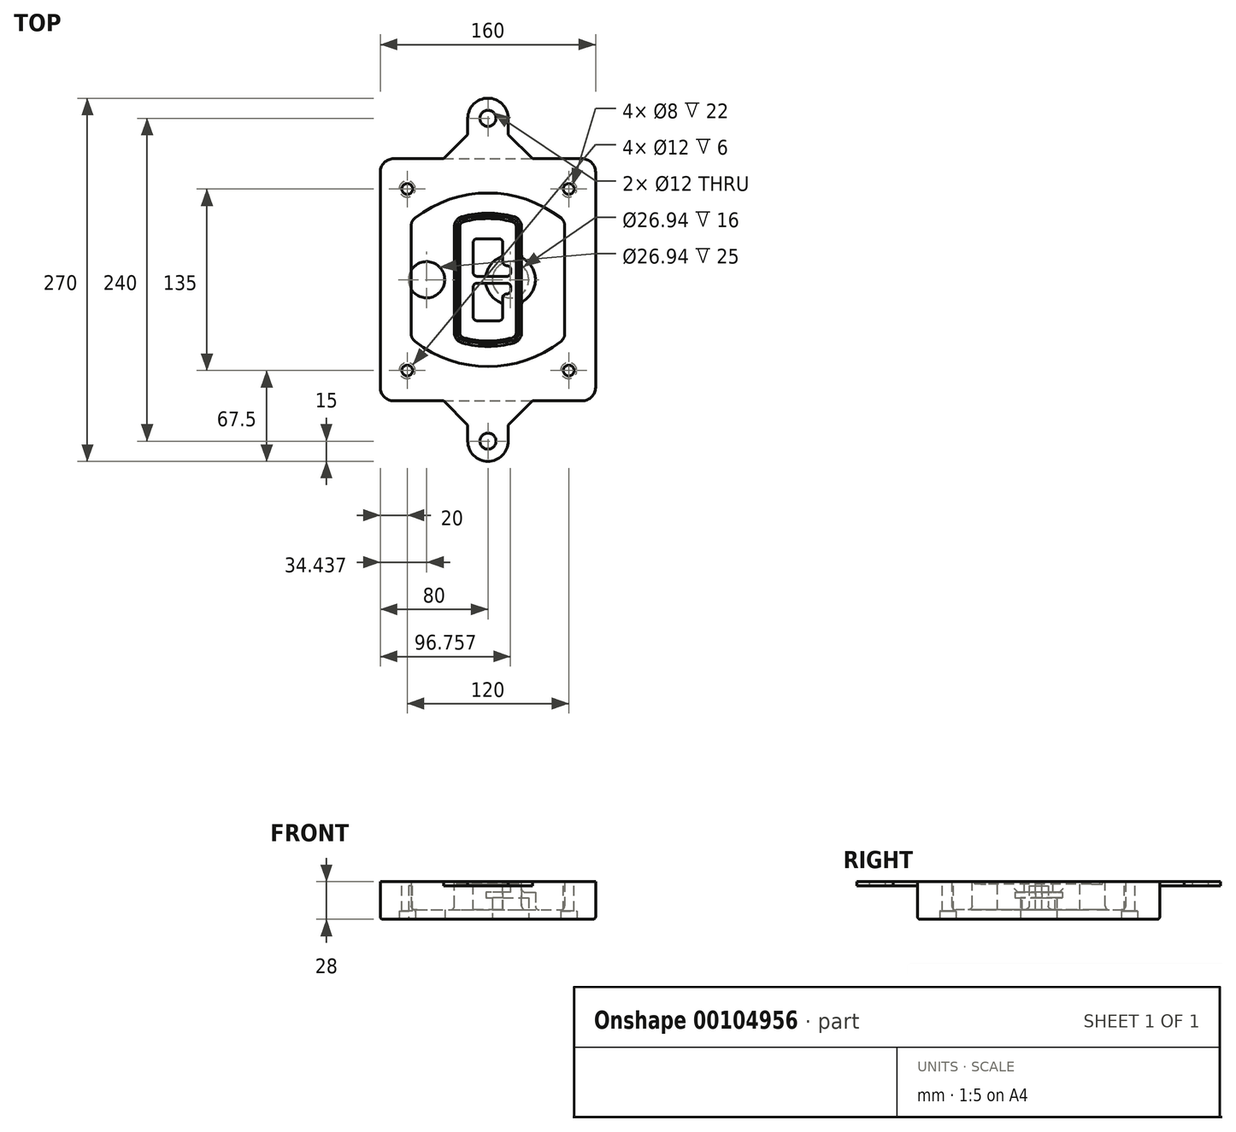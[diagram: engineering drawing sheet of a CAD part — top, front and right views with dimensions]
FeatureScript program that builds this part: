
annotation { "Feature Type Name" : "Feature", "Feature Type Description" : "" }
export const myFeature = defineFeature(function(context is Context, id is Id, definition is map)
    precondition{}
    {
        {
            var Q0;
            Q0=qCreatedBy(makeId("Top.planeOp"),FACE);
            var sketch = newSketch(context, id + "F0", { "sketchPlane" : qUnion([Q0])});
            skPoint(sketch, "E0.rect.middle", {"position": v(0, 0) * mm});
            skLineSegment(sketch, "E1.bottom", {"start": v(-70, -90) * mm, "end": v(70, -90) * mm});
            skLineSegment(sketch, "E1.top", {"start": v(-70, 90) * mm, "end": v(70, 90) * mm});
            skLineSegment(sketch, "E1.left", {"start": v(-80, -80) * mm, "end": v(-80, 80) * mm});
            skLineSegment(sketch, "E1.right", {"start": v(80, -80) * mm, "end": v(80, 80) * mm});
            skLineSegment(sketch, "E2", {"start": v(-80, 90) * mm, "end": v(80, -90) * mm, "construction": true});
            skLineSegment(sketch, "E3", {"start": v(80, 90) * mm, "end": v(-80, -90) * mm, "construction": true});
            skCircle(sketch, "E4", {"center": v(-60, 67.5) * mm, "radius": 4 * mm});
            skCircle(sketch, "E5", {"center": v(60, 67.5) * mm, "radius": 4 * mm});
            skCircle(sketch, "E6", {"center": v(60, -67.5) * mm, "radius": 4 * mm});
            skCircle(sketch, "E7", {"center": v(-60, -67.5) * mm, "radius": 4 * mm});
            skLineSegment(sketch, "E8", {"start": v(-60, 67.5) * mm, "end": v(60, 67.5) * mm, "construction": true});
            skLineSegment(sketch, "E9", {"start": v(60, 67.5) * mm, "end": v(60, -67.5) * mm, "construction": true});
            skLineSegment(sketch, "E10", {"start": v(60, -67.5) * mm, "end": v(-60, -67.5) * mm, "construction": true});
            skLineSegment(sketch, "E11", {"start": v(-60, -67.5) * mm, "end": v(-60, 67.5) * mm, "construction": true});
            skLineSegment(sketch, "E12", {"start": v(-60, 40.3) * mm, "end": v(-60, -40.3) * mm});
            skLineSegment(sketch, "E13", {"start": v(60, 40.3) * mm, "end": v(60, -40.3) * mm});
            skArc(sketch, "E14", {"start": v(56.15, 48.18) * mm, "mid": v(0, 67.5) * mm, "end": v(-56.15, 48.18) * mm});
            skArc(sketch, "E15", {"start": v(-56.15, -48.18) * mm, "mid": v(0, -67.5) * mm, "end": v(56.15, -48.18) * mm});
            skLineSegment(sketch, "E16", {"start": v(-60, 0) * mm, "end": v(60, 0) * mm, "construction": true});
            skPoint(sketch, "E17.visualSharp", {"position": v(-60, -45) * mm});
            skArc(sketch, "E17.filletArc", {"start": v(-60, -40.3) * mm, "mid": v(-58.99, -44.68) * mm, "end": v(-56.15, -48.18) * mm});
            skPoint(sketch, "E18.visualSharp", {"position": v(-60, 45) * mm});
            skArc(sketch, "E18.filletArc", {"start": v(-56.15, 48.18) * mm, "mid": v(-58.99, 44.68) * mm, "end": v(-60, 40.3) * mm});
            skPoint(sketch, "E19.visualSharp", {"position": v(60, 45) * mm});
            skArc(sketch, "E19.filletArc", {"start": v(60, 40.3) * mm, "mid": v(58.99, 44.68) * mm, "end": v(56.15, 48.18) * mm});
            skPoint(sketch, "E20.visualSharp", {"position": v(60, -45) * mm});
            skArc(sketch, "E20.filletArc", {"start": v(56.15, -48.18) * mm, "mid": v(58.99, -44.68) * mm, "end": v(60, -40.3) * mm});
            skPoint(sketch, "E21.visualSharp", {"position": v(-80, 90) * mm});
            skArc(sketch, "E21.filletArc", {"start": v(-70, 90) * mm, "mid": v(-77.07, 87.07) * mm, "end": v(-80, 80) * mm});
            skPoint(sketch, "E22.visualSharp", {"position": v(80, 90) * mm});
            skArc(sketch, "E22.filletArc", {"start": v(80, 80) * mm, "mid": v(77.07, 87.07) * mm, "end": v(70, 90) * mm});
            skPoint(sketch, "E23.visualSharp", {"position": v(80, -90) * mm});
            skArc(sketch, "E23.filletArc", {"start": v(70, -90) * mm, "mid": v(77.07, -87.07) * mm, "end": v(80, -80) * mm});
            skPoint(sketch, "E24.visualSharp", {"position": v(-80, -90) * mm});
            skArc(sketch, "E24.filletArc", {"start": v(-80, -80) * mm, "mid": v(-77.07, -87.07) * mm, "end": v(-70, -90) * mm});
            skArc(sketch, "E25.0", {"start": v(57, 40.3) * mm, "mid": v(56.3, 43.36) * mm, "end": v(54.3, 45.81) * mm});
            skLineSegment(sketch, "E25.1", {"start": v(57, 40.3) * mm, "end": v(57, -40.3) * mm});
            skArc(sketch, "E25.2", {"start": v(54.3, -45.81) * mm, "mid": v(56.3, -43.36) * mm, "end": v(57, -40.3) * mm});
            skArc(sketch, "E25.3", {"start": v(-54.3, -45.81) * mm, "mid": v(0, -64.5) * mm, "end": v(54.3, -45.81) * mm});
            skArc(sketch, "E25.4", {"start": v(-57, -40.3) * mm, "mid": v(-56.3, -43.36) * mm, "end": v(-54.3, -45.81) * mm});
            skArc(sketch, "E25.5", {"start": v(54.3, 45.81) * mm, "mid": v(0, 64.5) * mm, "end": v(-54.3, 45.81) * mm});
            skLineSegment(sketch, "E25.6", {"start": v(-57, 40.3) * mm, "end": v(-57, -40.3) * mm});
            skArc(sketch, "E25.7", {"start": v(-54.3, 45.81) * mm, "mid": v(-56.3, 43.36) * mm, "end": v(-57, 40.3) * mm});
            skArc(sketch, "E26.0", {"start": v(-58.62, 51.33) * mm, "mid": v(-62.58, 46.43) * mm, "end": v(-64, 40.3) * mm});
            skArc(sketch, "E26.1", {"start": v(58.62, 51.33) * mm, "mid": v(0, 71.5) * mm, "end": v(-58.62, 51.33) * mm});
            skArc(sketch, "E26.2", {"start": v(64, 40.3) * mm, "mid": v(62.58, 46.43) * mm, "end": v(58.62, 51.33) * mm});
            skLineSegment(sketch, "E26.3", {"start": v(64, 40.3) * mm, "end": v(64, -40.3) * mm});
            skArc(sketch, "E26.4", {"start": v(58.62, -51.33) * mm, "mid": v(62.58, -46.43) * mm, "end": v(64, -40.3) * mm});
            skLineSegment(sketch, "E26.5", {"start": v(-64, 40.3) * mm, "end": v(-64, -40.3) * mm});
            skArc(sketch, "E26.6", {"start": v(-58.62, -51.33) * mm, "mid": v(0, -71.5) * mm, "end": v(58.62, -51.33) * mm});
            skArc(sketch, "E26.7", {"start": v(-64, -40.3) * mm, "mid": v(-62.58, -46.43) * mm, "end": v(-58.62, -51.33) * mm});
            skSolve(sketch);
        }
        {
            var Q0;
            Q0=makeQuery(id+"F0.imprint","IMPRINT",FACE,{"disambiguationData":[TD([[makeQuery(id+"F0.imprint","IMPRINT",EDGE,{"derivedFrom":sQuery(id+"F0.wireOp",EDGE,"E1.bottom")}),1.0]])]});
            var Q1;
            Q1=makeQuery(id+"F0.imprint","IMPRINT",FACE,{"disambiguationData":[TD([[makeQuery(id+"F0.imprint","IMPRINT",EDGE,{"derivedFrom":sQuery(id+"F0.wireOp",EDGE,"E12")}),1.0]])]});
            var Q2;
            Q2=makeQuery(id+"F0.imprint","IMPRINT",FACE,{"disambiguationData":[TD([[makeQuery(id+"F0.imprint","IMPRINT",EDGE,{"derivedFrom":sQuery(id+"F0.wireOp",EDGE,"E25.0")}),1.0]])]});
            var Q3;
            Q3=makeQuery(id+"F0.imprint","IMPRINT",FACE,{"disambiguationData":[TD([[makeQuery(id+"F0.imprint","IMPRINT",EDGE,{"derivedFrom":sQuery(id+"F0.wireOp",EDGE,"E12")}),-1.0]])]});
            extrude(context, id + "F1", {"entities" : qUnion([Q0, Q1, Q2, Q3]), "oppositeDirection" : true, "depth" : 25 * mm});
        }
        {
            var Q0;
            Q0=makeQuery(id+"F0.imprint","IMPRINT",FACE,{"disambiguationData":[TD([[makeQuery(id+"F0.imprint","IMPRINT",EDGE,{"derivedFrom":sQuery(id+"F0.wireOp",EDGE,"E12")}),1.0]])]});
            extrude(context, id + "F2", {"entities" : qUnion([Q0]), "operationType" : NewBodyOperationType.ADD, "depth" : 3 * mm});
        }
        {
            var Q0;
            Q0=makeQuery(id+"F0.imprint","IMPRINT",FACE,{"disambiguationData":[TD([[makeQuery(id+"F0.imprint","IMPRINT",EDGE,{"derivedFrom":sQuery(id+"F0.wireOp",EDGE,"E25.0")}),1.0]])]});
            extrude(context, id + "F3", {"entities" : qUnion([Q0]), "operationType" : NewBodyOperationType.REMOVE, "oppositeDirection" : true, "depth" : 18 * mm});
        }
        {
            var Q0;
            Q0=makeQuery(id+"F2.opExtrude","CAP_FACE",FACE,{"disambiguationData":[OSD([sQuery(id+"F0.wireOp",EDGE,"E12"),sQuery(id+"F0.wireOp",EDGE,"E13"),sQuery(id+"F0.wireOp",EDGE,"E14"),sQuery(id+"F0.wireOp",EDGE,"E15"),sQuery(id+"F0.wireOp",EDGE,"E17.filletArc"),sQuery(id+"F0.wireOp",EDGE,"E18.filletArc"),sQuery(id+"F0.wireOp",EDGE,"E19.filletArc"),sQuery(id+"F0.wireOp",EDGE,"E20.filletArc"),sQuery(id+"F0.wireOp",EDGE,"E25.0"),sQuery(id+"F0.wireOp",EDGE,"E25.1"),sQuery(id+"F0.wireOp",EDGE,"E25.2"),sQuery(id+"F0.wireOp",EDGE,"E25.3"),sQuery(id+"F0.wireOp",EDGE,"E25.4"),sQuery(id+"F0.wireOp",EDGE,"E25.5"),sQuery(id+"F0.wireOp",EDGE,"E25.6"),sQuery(id+"F0.wireOp",EDGE,"E25.7")])],"isStart":false});
            var sketch = newSketch(context, id + "F4", { "sketchPlane" : qUnion([Q0])});
            skArc(sketch, "E27.0", {"start": v(-19.08, -46.97) * mm, "mid": v(0, -49.5) * mm, "end": v(19.08, -46.97) * mm});
            skArc(sketch, "E28.0", {"start": v(19.08, 46.97) * mm, "mid": v(0, 49.5) * mm, "end": v(-19.08, 46.97) * mm});
            skLineSegment(sketch, "E29", {"start": v(-25, 39.25) * mm, "end": v(-25, -39.25) * mm});
            skLineSegment(sketch, "E30", {"start": v(25, 39.25) * mm, "end": v(25, -39.25) * mm});
            skLineSegment(sketch, "E31", {"start": v(-25, 45.1) * mm, "end": v(25, 45.1) * mm, "construction": true});
            skLineSegment(sketch, "E32", {"start": v(-25, -45.1) * mm, "end": v(25, -45.1) * mm, "construction": true});
            skPoint(sketch, "E33.visualSharp", {"position": v(-25, 45.1) * mm});
            skArc(sketch, "E33.filletArc", {"start": v(-19.08, 46.97) * mm, "mid": v(-23.35, 44.11) * mm, "end": v(-25, 39.25) * mm});
            skPoint(sketch, "E34.visualSharp", {"position": v(25, 45.1) * mm});
            skArc(sketch, "E34.filletArc", {"start": v(25, 39.25) * mm, "mid": v(23.35, 44.11) * mm, "end": v(19.08, 46.97) * mm});
            skPoint(sketch, "E35.visualSharp", {"position": v(25, -45.1) * mm});
            skArc(sketch, "E35.filletArc", {"start": v(19.08, -46.97) * mm, "mid": v(23.35, -44.11) * mm, "end": v(25, -39.25) * mm});
            skPoint(sketch, "E36.visualSharp", {"position": v(-25, -45.1) * mm});
            skArc(sketch, "E36.filletArc", {"start": v(-25, -39.25) * mm, "mid": v(-23.35, -44.11) * mm, "end": v(-19.08, -46.97) * mm});
            skArc(sketch, "E37.0", {"start": v(54.3, 45.81) * mm, "mid": v(0, 64.5) * mm, "end": v(-54.3, 45.81) * mm});
            skArc(sketch, "E37.1", {"start": v(-54.3, 45.81) * mm, "mid": v(-56.3, 43.36) * mm, "end": v(-57, 40.3) * mm});
            skLineSegment(sketch, "E37.2", {"start": v(-57, 40.3) * mm, "end": v(-57, -40.3) * mm});
            skArc(sketch, "E37.3", {"start": v(-57, -40.3) * mm, "mid": v(-56.3, -43.36) * mm, "end": v(-54.3, -45.81) * mm});
            skArc(sketch, "E37.4", {"start": v(-54.3, -45.81) * mm, "mid": v(0, -64.5) * mm, "end": v(54.3, -45.81) * mm});
            skArc(sketch, "E37.5", {"start": v(54.3, -45.81) * mm, "mid": v(56.3, -43.36) * mm, "end": v(57, -40.3) * mm});
            skLineSegment(sketch, "E37.6", {"start": v(57, 40.3) * mm, "end": v(57, -40.3) * mm});
            skArc(sketch, "E37.7", {"start": v(57, 40.3) * mm, "mid": v(56.3, 43.36) * mm, "end": v(54.3, 45.81) * mm});
            skLineSegment(sketch, "E38.0", {"start": v(23, 39.25) * mm, "end": v(23, -39.25) * mm});
            skArc(sketch, "E38.1", {"start": v(18.56, -45.04) * mm, "mid": v(21.76, -42.9) * mm, "end": v(23, -39.25) * mm});
            skArc(sketch, "E38.2", {"start": v(-18.56, -45.04) * mm, "mid": v(0, -47.5) * mm, "end": v(18.56, -45.04) * mm});
            skArc(sketch, "E38.3", {"start": v(-23, -39.25) * mm, "mid": v(-21.76, -42.9) * mm, "end": v(-18.56, -45.04) * mm});
            skLineSegment(sketch, "E38.4", {"start": v(-23, 39.25) * mm, "end": v(-23, -39.25) * mm});
            skArc(sketch, "E38.5", {"start": v(23, 39.25) * mm, "mid": v(21.76, 42.9) * mm, "end": v(18.56, 45.04) * mm});
            skArc(sketch, "E38.6", {"start": v(-18.56, 45.04) * mm, "mid": v(-21.76, 42.9) * mm, "end": v(-23, 39.25) * mm});
            skArc(sketch, "E38.7", {"start": v(18.56, 45.04) * mm, "mid": v(0, 47.5) * mm, "end": v(-18.56, 45.04) * mm});
            skArc(sketch, "E39.0", {"start": v(21, 39.25) * mm, "mid": v(20.18, 41.68) * mm, "end": v(18.04, 43.1) * mm});
            skLineSegment(sketch, "E39.1", {"start": v(21, 39.25) * mm, "end": v(21, -39.25) * mm});
            skArc(sketch, "E39.2", {"start": v(18.04, -43.1) * mm, "mid": v(20.18, -41.68) * mm, "end": v(21, -39.25) * mm});
            skArc(sketch, "E39.3", {"start": v(-18.04, -43.1) * mm, "mid": v(0, -45.5) * mm, "end": v(18.04, -43.1) * mm});
            skArc(sketch, "E39.4", {"start": v(-21, -39.25) * mm, "mid": v(-20.18, -41.68) * mm, "end": v(-18.04, -43.1) * mm});
            skArc(sketch, "E39.5", {"start": v(18.04, 43.1) * mm, "mid": v(0, 45.5) * mm, "end": v(-18.04, 43.1) * mm});
            skLineSegment(sketch, "E39.6", {"start": v(-21, 39.25) * mm, "end": v(-21, -39.25) * mm});
            skArc(sketch, "E39.7", {"start": v(-18.04, 43.1) * mm, "mid": v(-20.18, 41.68) * mm, "end": v(-21, 39.25) * mm});
            skLineSegment(sketch, "E40", {"start": v(-25, 0) * mm, "end": v(25, 0) * mm, "construction": true});
            skLineSegment(sketch, "E41", {"start": v(-11, 5.5) * mm, "end": v(-11, 27.5) * mm});
            skLineSegment(sketch, "E42", {"start": v(-8, 30.5) * mm, "end": v(8, 30.5) * mm});
            skLineSegment(sketch, "E43", {"start": v(11, 27.5) * mm, "end": v(11, 13.5) * mm});
            skLineSegment(sketch, "E44", {"start": v(14, 10.5) * mm, "end": v(14, 10.5) * mm});
            skLineSegment(sketch, "E45", {"start": v(17, 7.5) * mm, "end": v(17, 5.5) * mm});
            skLineSegment(sketch, "E46", {"start": v(14, 2.5) * mm, "end": v(-8, 2.5) * mm});
            skPoint(sketch, "E47.visualSharp", {"position": v(-11, 30.5) * mm});
            skArc(sketch, "E47.filletArc", {"start": v(-8, 30.5) * mm, "mid": v(-10.12, 29.62) * mm, "end": v(-11, 27.5) * mm});
            skPoint(sketch, "E48.visualSharp", {"position": v(11, 30.5) * mm});
            skArc(sketch, "E48.filletArc", {"start": v(11, 27.5) * mm, "mid": v(10.12, 29.62) * mm, "end": v(8, 30.5) * mm});
            skPoint(sketch, "E49.visualSharp", {"position": v(11, 10.5) * mm});
            skArc(sketch, "E49.filletArc", {"start": v(11, 13.5) * mm, "mid": v(11.88, 11.38) * mm, "end": v(14, 10.5) * mm});
            skPoint(sketch, "E50.visualSharp", {"position": v(17, 10.5) * mm});
            skArc(sketch, "E50.filletArc", {"start": v(17, 7.5) * mm, "mid": v(16.12, 9.62) * mm, "end": v(14, 10.5) * mm});
            skPoint(sketch, "E51.visualSharp", {"position": v(17, 2.5) * mm});
            skArc(sketch, "E51.filletArc", {"start": v(14, 2.5) * mm, "mid": v(16.12, 3.38) * mm, "end": v(17, 5.5) * mm});
            skPoint(sketch, "E52.visualSharp", {"position": v(-11, 2.5) * mm});
            skArc(sketch, "E52.filletArc", {"start": v(-11, 5.5) * mm, "mid": v(-10.12, 3.38) * mm, "end": v(-8, 2.5) * mm});
            skLineSegment(sketch, "E53.0.MirrorCS", {"start": v(14, -2.5) * mm, "end": v(-8, -2.5) * mm});
            skArc(sketch, "E54.0.MirrorCS", {"start": v(-11, -5.5) * mm, "mid": v(-10.12, -3.38) * mm, "end": v(-8, -2.5) * mm});
            skLineSegment(sketch, "E55.0.MirrorCS", {"start": v(-11, -5.5) * mm, "end": v(-11, -27.5) * mm});
            skArc(sketch, "E56.0.MirrorCS", {"start": v(-8, -30.5) * mm, "mid": v(-10.12, -29.62) * mm, "end": v(-11, -27.5) * mm});
            skLineSegment(sketch, "E57.0.MirrorCS", {"start": v(-8, -30.5) * mm, "end": v(8, -30.5) * mm});
            skArc(sketch, "E58.0.MirrorCS", {"start": v(11, -27.5) * mm, "mid": v(10.12, -29.62) * mm, "end": v(8, -30.5) * mm});
            skLineSegment(sketch, "E59.0.MirrorCS", {"start": v(11, -27.5) * mm, "end": v(11, -13.5) * mm});
            skArc(sketch, "E60.0.MirrorCS", {"start": v(11, -13.5) * mm, "mid": v(11.88, -11.38) * mm, "end": v(14, -10.5) * mm});
            skArc(sketch, "E61.0.MirrorCS", {"start": v(17, -7.5) * mm, "mid": v(16.12, -9.62) * mm, "end": v(14, -10.5) * mm});
            skLineSegment(sketch, "E62.0.MirrorCS", {"start": v(17, -7.5) * mm, "end": v(17, -5.5) * mm});
            skArc(sketch, "E63.0.MirrorCS", {"start": v(14, -2.5) * mm, "mid": v(16.12, -3.38) * mm, "end": v(17, -5.5) * mm});
            skSolve(sketch);
        }
        {
            var Q0;
            Q0=makeQuery(id+"F4.imprint","IMPRINT",FACE,{"disambiguationData":[TD([[makeQuery(id+"F4.imprint","IMPRINT",EDGE,{"derivedFrom":sQuery(id+"F4.wireOp",EDGE,"E27.0")}),1.0]])]});
            var Q1;
            Q1=makeQuery(id+"F4.imprint","IMPRINT",FACE,{"disambiguationData":[TD([[makeQuery(id+"F4.imprint","IMPRINT",EDGE,{"derivedFrom":sQuery(id+"F4.wireOp",EDGE,"E38.0")}),-1.0]])]});
            var Q2;
            Q2=makeQuery(id+"F4.imprint","IMPRINT",FACE,{"disambiguationData":[TD([[makeQuery(id+"F4.imprint","IMPRINT",EDGE,{"derivedFrom":sQuery(id+"F4.wireOp",EDGE,"E39.0")}),1.0]])]});
            extrude(context, id + "F5", {"entities" : qUnion([Q0, Q1, Q2]), "operationType" : NewBodyOperationType.ADD, "endBound" : BoundingType.UP_TO_NEXT, "oppositeDirection" : true, "depth" : 25 * mm});
        }
        {
            var Q0;
            Q0=makeQuery(id+"F4.imprint","IMPRINT",FACE,{"disambiguationData":[TD([[makeQuery(id+"F4.imprint","IMPRINT",EDGE,{"derivedFrom":sQuery(id+"F4.wireOp",EDGE,"E38.0")}),-1.0]])]});
            extrude(context, id + "F6", {"entities" : qUnion([Q0]), "operationType" : NewBodyOperationType.REMOVE, "oppositeDirection" : true, "depth" : 2 * mm});
        }
        {
            var Q0;
            Q0=makeQuery(id+"F1.opExtrude","CAP_FACE",FACE,{"disambiguationData":[OSD([sQuery(id+"F0.wireOp",EDGE,"E1.bottom"),sQuery(id+"F0.wireOp",EDGE,"E1.top"),sQuery(id+"F0.wireOp",EDGE,"E1.left"),sQuery(id+"F0.wireOp",EDGE,"E1.right"),sQuery(id+"F0.wireOp",EDGE,"E4"),sQuery(id+"F0.wireOp",EDGE,"E5"),sQuery(id+"F0.wireOp",EDGE,"E6"),sQuery(id+"F0.wireOp",EDGE,"E7"),sQuery(id+"F0.wireOp",EDGE,"E21.filletArc"),sQuery(id+"F0.wireOp",EDGE,"E22.filletArc"),sQuery(id+"F0.wireOp",EDGE,"E23.filletArc"),sQuery(id+"F0.wireOp",EDGE,"E24.filletArc")])],"isStart":false});
            var sketch = newSketch(context, id + "F7", { "sketchPlane" : qUnion([Q0])});
            skCircle(sketch, "E64", {"center": v(16.76, 0) * mm, "radius": 13.47 * mm});
            skCircle(sketch, "E65", {"center": v(-45.56, 0) * mm, "radius": 13.47 * mm});
            skLineSegment(sketch, "E66", {"start": v(80, 0) * mm, "end": v(-80, 0) * mm});
            skCircle(sketch, "E67", {"center": v(16.76, 0) * mm, "radius": 18.47 * mm});
            skCircle(sketch, "E68", {"center": v(60, -67.5) * mm, "radius": 6 * mm});
            skCircle(sketch, "E69", {"center": v(-60, -67.5) * mm, "radius": 6 * mm});
            skCircle(sketch, "E70", {"center": v(-60, 67.5) * mm, "radius": 6 * mm});
            skCircle(sketch, "E71", {"center": v(60, 67.5) * mm, "radius": 6 * mm});
            skSolve(sketch);
        }
        {
            var Q0;
            {var subQ1=sQuery(id+"F7.wireOp",EDGE,"E66");var subQ4=sQuery(id+"F7.wireOp",EDGE,"E64");var subQ6=makeQuery(id+"F7.imprint","INTERSECT",VERTEX,{"disambiguationData":[OD(0.0)],"derivedFrom":[subQ4,subQ1]});Q0=makeQuery(id+"F7.imprint","IMPRINT",FACE,{"disambiguationData":[TD([[makeQuery(id+"F7.imprint","IMPRINT",EDGE,{"disambiguationData":[TD([[subQ6,-1.0]])],"derivedFrom":subQ4}),-1.0]])]});}
            var Q1;
            {var subQ0=sQuery(id+"F7.wireOp",EDGE,"E66");var subQ1=sQuery(id+"F7.wireOp",EDGE,"E64");var subQ3=makeQuery(id+"F7.imprint","INTERSECT",VERTEX,{"disambiguationData":[OD(0.0)],"derivedFrom":[subQ1,subQ0]});Q1=makeQuery(id+"F7.imprint","IMPRINT",FACE,{"disambiguationData":[TD([[makeQuery(id+"F7.imprint","IMPRINT",EDGE,{"disambiguationData":[TD([[subQ3,-1.0]])],"derivedFrom":subQ1}),1.0]])]});}
            var Q2;
            {var subQ0=sQuery(id+"F7.wireOp",EDGE,"E66");var subQ1=sQuery(id+"F7.wireOp",EDGE,"E64");var subQ3=makeQuery(id+"F7.imprint","INTERSECT",VERTEX,{"disambiguationData":[OD(0.0)],"derivedFrom":[subQ1,subQ0]});Q2=makeQuery(id+"F7.imprint","IMPRINT",FACE,{"disambiguationData":[TD([[makeQuery(id+"F7.imprint","IMPRINT",EDGE,{"disambiguationData":[TD([[subQ3,1.0]])],"derivedFrom":subQ1}),1.0]])]});}
            var Q3;
            {var subQ1=sQuery(id+"F7.wireOp",EDGE,"E66");var subQ4=sQuery(id+"F7.wireOp",EDGE,"E64");var subQ6=makeQuery(id+"F7.imprint","INTERSECT",VERTEX,{"disambiguationData":[OD(0.0)],"derivedFrom":[subQ4,subQ1]});Q3=makeQuery(id+"F7.imprint","IMPRINT",FACE,{"disambiguationData":[TD([[makeQuery(id+"F7.imprint","IMPRINT",EDGE,{"disambiguationData":[TD([[subQ6,1.0]])],"derivedFrom":subQ4}),-1.0]])]});}
            extrude(context, id + "F8", {"entities" : qUnion([Q0, Q1, Q2, Q3]), "operationType" : NewBodyOperationType.ADD, "oppositeDirection" : true, "depth" : 20 * mm});
        }
        {
            var Q0;
            {var subQ0=sQuery(id+"F7.wireOp",EDGE,"E66");var subQ1=sQuery(id+"F7.wireOp",EDGE,"E64");var subQ3=makeQuery(id+"F7.imprint","INTERSECT",VERTEX,{"disambiguationData":[OD(0.0)],"derivedFrom":[subQ1,subQ0]});Q0=makeQuery(id+"F7.imprint","IMPRINT",FACE,{"disambiguationData":[TD([[makeQuery(id+"F7.imprint","IMPRINT",EDGE,{"disambiguationData":[TD([[subQ3,-1.0]])],"derivedFrom":subQ1}),1.0]])]});}
            var Q1;
            {var subQ0=sQuery(id+"F7.wireOp",EDGE,"E66");var subQ1=sQuery(id+"F7.wireOp",EDGE,"E64");var subQ3=makeQuery(id+"F7.imprint","INTERSECT",VERTEX,{"disambiguationData":[OD(0.0)],"derivedFrom":[subQ1,subQ0]});Q1=makeQuery(id+"F7.imprint","IMPRINT",FACE,{"disambiguationData":[TD([[makeQuery(id+"F7.imprint","IMPRINT",EDGE,{"disambiguationData":[TD([[subQ3,1.0]])],"derivedFrom":subQ1}),1.0]])]});}
            extrude(context, id + "F9", {"entities" : qUnion([Q0, Q1]), "operationType" : NewBodyOperationType.REMOVE, "oppositeDirection" : true, "depth" : 16 * mm});
        }
        {
            var Q0;
            {var subQ0=sQuery(id+"F7.wireOp",EDGE,"E66");var subQ1=sQuery(id+"F7.wireOp",EDGE,"E65");var subQ3=makeQuery(id+"F7.imprint","INTERSECT",VERTEX,{"disambiguationData":[OD(0.0)],"derivedFrom":[subQ1,subQ0]});Q0=makeQuery(id+"F7.imprint","IMPRINT",FACE,{"disambiguationData":[TD([[makeQuery(id+"F7.imprint","IMPRINT",EDGE,{"disambiguationData":[TD([[subQ3,-1.0]])],"derivedFrom":subQ1}),1.0]])]});}
            var Q1;
            {var subQ0=sQuery(id+"F7.wireOp",EDGE,"E66");var subQ1=sQuery(id+"F7.wireOp",EDGE,"E65");var subQ3=makeQuery(id+"F7.imprint","INTERSECT",VERTEX,{"disambiguationData":[OD(0.0)],"derivedFrom":[subQ1,subQ0]});Q1=makeQuery(id+"F7.imprint","IMPRINT",FACE,{"disambiguationData":[TD([[makeQuery(id+"F7.imprint","IMPRINT",EDGE,{"disambiguationData":[TD([[subQ3,1.0]])],"derivedFrom":subQ1}),1.0]])]});}
            extrude(context, id + "F10", {"entities" : qUnion([Q0, Q1]), "operationType" : NewBodyOperationType.REMOVE, "oppositeDirection" : true, "depth" : 25 * mm});
        }
        {
            var Q0;
            Q0=makeQuery(id+"F7.imprint","IMPRINT",FACE,{"disambiguationData":[TD([[makeQuery(id+"F7.imprint","IMPRINT",EDGE,{"derivedFrom":sQuery(id+"F7.wireOp",EDGE,"E68")}),1.0]])]});
            var Q1;
            Q1=makeQuery(id+"F7.imprint","IMPRINT",FACE,{"disambiguationData":[TD([[makeQuery(id+"F7.imprint","IMPRINT",EDGE,{"derivedFrom":makeQuery(id+"F1.opExtrude","CAP_EDGE",EDGE,{"disambiguationData":[OSD([sQuery(id+"F0.wireOp",EDGE,"E5")])],"isStart":false})}),-1.0]])]});
            var Q2;
            Q2=makeQuery(id+"F7.imprint","IMPRINT",FACE,{"disambiguationData":[TD([[makeQuery(id+"F7.imprint","IMPRINT",EDGE,{"derivedFrom":sQuery(id+"F7.wireOp",EDGE,"E69")}),1.0]])]});
            var Q3;
            Q3=makeQuery(id+"F7.imprint","IMPRINT",FACE,{"disambiguationData":[TD([[makeQuery(id+"F7.imprint","IMPRINT",EDGE,{"derivedFrom":makeQuery(id+"F1.opExtrude","CAP_EDGE",EDGE,{"disambiguationData":[OSD([sQuery(id+"F0.wireOp",EDGE,"E4")])],"isStart":false})}),-1.0]])]});
            var Q4;
            Q4=makeQuery(id+"F7.imprint","IMPRINT",FACE,{"disambiguationData":[TD([[makeQuery(id+"F7.imprint","IMPRINT",EDGE,{"derivedFrom":sQuery(id+"F7.wireOp",EDGE,"E70")}),1.0]])]});
            var Q5;
            Q5=makeQuery(id+"F7.imprint","IMPRINT",FACE,{"disambiguationData":[TD([[makeQuery(id+"F7.imprint","IMPRINT",EDGE,{"derivedFrom":makeQuery(id+"F1.opExtrude","CAP_EDGE",EDGE,{"disambiguationData":[OSD([sQuery(id+"F0.wireOp",EDGE,"E7")])],"isStart":false})}),-1.0]])]});
            var Q6;
            Q6=makeQuery(id+"F7.imprint","IMPRINT",FACE,{"disambiguationData":[TD([[makeQuery(id+"F7.imprint","IMPRINT",EDGE,{"derivedFrom":sQuery(id+"F7.wireOp",EDGE,"E71")}),1.0]])]});
            var Q7;
            Q7=makeQuery(id+"F7.imprint","IMPRINT",FACE,{"disambiguationData":[TD([[makeQuery(id+"F7.imprint","IMPRINT",EDGE,{"derivedFrom":makeQuery(id+"F1.opExtrude","CAP_EDGE",EDGE,{"disambiguationData":[OSD([sQuery(id+"F0.wireOp",EDGE,"E6")])],"isStart":false})}),-1.0]])]});
            extrude(context, id + "F11", {"entities" : qUnion([Q0, Q1, Q2, Q3, Q4, Q5, Q6, Q7]), "operationType" : NewBodyOperationType.REMOVE, "oppositeDirection" : true, "depth" : 6 * mm});
        }
        {
            var Q0;
            Q0=makeQuery(id+"F9.boolean.opBoolean","COPY",FACE,{"derivedFrom":makeQuery(id+"F9.opExtrude","CAP_FACE",FACE,{"disambiguationData":[OSD([sQuery(id+"F7.wireOp",EDGE,"E64")])],"isStart":false})});
            var sketch = newSketch(context, id + "F12", { "sketchPlane" : qUnion([Q0])});
            skArc(sketch, "E72.0", {"start": v(11, 17.55) * mm, "mid": v(2.57, 11.82) * mm, "end": v(-1.54, 2.5) * mm});
            skArc(sketch, "E72.1", {"start": v(-1.54, -2.5) * mm, "mid": v(2.57, -11.82) * mm, "end": v(11, -17.55) * mm});
            skLineSegment(sketch, "E73", {"start": v(-1.54, -2.5) * mm, "end": v(14, -2.5) * mm});
            skLineSegment(sketch, "E74.0", {"start": v(14, 2.5) * mm, "end": v(-1.54, 2.5) * mm});
            skArc(sketch, "E74.1", {"start": v(14, 2.5) * mm, "mid": v(16.12, 3.38) * mm, "end": v(17, 5.5) * mm});
            skLineSegment(sketch, "E74.2", {"start": v(17, 7.5) * mm, "end": v(17, 5.5) * mm});
            skArc(sketch, "E74.3", {"start": v(17, 7.5) * mm, "mid": v(16.12, 9.62) * mm, "end": v(14, 10.5) * mm});
            skArc(sketch, "E74.4", {"start": v(11, 13.5) * mm, "mid": v(11.88, 11.38) * mm, "end": v(14, 10.5) * mm});
            skLineSegment(sketch, "E74.5", {"start": v(11, 17.55) * mm, "end": v(11, 13.5) * mm});
            skLineSegment(sketch, "E74.7", {"start": v(14, -2.5) * mm, "end": v(-1.54, -2.5) * mm});
            skArc(sketch, "E74.8", {"start": v(14, -2.5) * mm, "mid": v(16.12, -3.38) * mm, "end": v(17, -5.5) * mm});
            skLineSegment(sketch, "E74.9", {"start": v(17, -7.5) * mm, "end": v(17, -5.5) * mm});
            skArc(sketch, "E74.10", {"start": v(17, -7.5) * mm, "mid": v(16.12, -9.62) * mm, "end": v(14, -10.5) * mm});
            skArc(sketch, "E74.11", {"start": v(11, -13.5) * mm, "mid": v(11.88, -11.38) * mm, "end": v(14, -10.5) * mm});
            skLineSegment(sketch, "E74.12", {"start": v(11, -17.55) * mm, "end": v(11, -13.5) * mm});
            skPoint(sketch, "E75.orphan", {"position": v(11, -27.5) * mm});
            skPoint(sketch, "E76.orphan", {"position": v(-8, -2.5) * mm});
            skPoint(sketch, "E77.orphan", {"position": v(-8, 2.5) * mm});
            skPoint(sketch, "E78.orphan", {"position": v(11, 27.5) * mm});
            skSolve(sketch);
        }
        {
            var Q0;
            {var subQ7=sQuery(id+"F12.wireOp",EDGE,"E72.0");var subQ14=sQuery(id+"F12.wireOp",EDGE,"E72.1");var subQ16=sQuery(id+"F12.wireOp",EDGE,"E74.1");var subQ18=sQuery(id+"F12.wireOp",EDGE,"E74.8");Q0=qUnion([makeQuery(id+"F12.imprint","IMPRINT",FACE,{"disambiguationData":[TD([[makeQuery(id+"F12.imprint","IMPRINT",EDGE,{"derivedFrom":subQ7}),1.0]])]}),makeQuery(id+"F12.imprint","IMPRINT",FACE,{"disambiguationData":[TD([[makeQuery(id+"F12.imprint","IMPRINT",EDGE,{"derivedFrom":subQ14}),1.0]])]}),makeQuery(id+"F12.imprint","IMPRINT",FACE,{"disambiguationData":[TD([[makeQuery(id+"F12.imprint","IMPRINT",EDGE,{"derivedFrom":subQ16}),1.0]])]}),makeQuery(id+"F12.imprint","IMPRINT",FACE,{"disambiguationData":[TD([[makeQuery(id+"F12.imprint","IMPRINT",EDGE,{"derivedFrom":subQ18}),-1.0]])]})]);}
            var Q1;
            Q1=makeQuery(id+"F5.boolean.opBoolean","SPLIT",FACE,{"disambiguationData":[TD([makeQuery(id+"F5.opExtrude","SWEPT_FACE",FACE,{"disambiguationData":[OSD([sQuery(id+"F4.wireOp",EDGE,"E41")])]})])],"derivedFrom":makeQuery(id+"F3.boolean.opBoolean","COPY",FACE,{"derivedFrom":makeQuery(id+"F3.opExtrude","CAP_FACE",FACE,{"disambiguationData":[OSD([sQuery(id+"F0.wireOp",EDGE,"E25.0"),sQuery(id+"F0.wireOp",EDGE,"E25.1"),sQuery(id+"F0.wireOp",EDGE,"E25.2"),sQuery(id+"F0.wireOp",EDGE,"E25.3"),sQuery(id+"F0.wireOp",EDGE,"E25.4"),sQuery(id+"F0.wireOp",EDGE,"E25.5"),sQuery(id+"F0.wireOp",EDGE,"E25.6"),sQuery(id+"F0.wireOp",EDGE,"E25.7")])],"isStart":false})})});
            extrude(context, id + "F13", {"entities" : qUnion([Q0]), "operationType" : NewBodyOperationType.REMOVE, "endBound" : BoundingType.UP_TO_SURFACE, "endBoundEntityFace" : qUnion([Q1]), "depth" : 25 * mm});
        }
        {
            var Q0;
            Q0=makeQuery(id+"F3.boolean.opBoolean","COPY",EDGE,{"derivedFrom":makeQuery(id+"F3.opExtrude","CAP_EDGE",EDGE,{"disambiguationData":[OSD([sQuery(id+"F0.wireOp",EDGE,"E25.6")])],"isStart":false})});
            var Q1;
            Q1=makeQuery(id+"F8.boolean.opBoolean","INTERSECT",EDGE,{"derivedFrom":[makeQuery(id+"F5.opExtrude","SWEPT_FACE",FACE,{"disambiguationData":[OSD([sQuery(id+"F4.wireOp",EDGE,"E30")])]}),makeQuery(id+"F8.opExtrude","CAP_FACE",FACE,{"disambiguationData":[OSD([sQuery(id+"F7.wireOp",EDGE,"E67")])],"isStart":false})]});
            var Q2;
            Q2=makeQuery(id+"F8.boolean.opBoolean","INTERSECT",EDGE,{"disambiguationData":[OD(1.0)],"derivedFrom":[makeQuery(id+"F5.opExtrude","SWEPT_FACE",FACE,{"disambiguationData":[OSD([sQuery(id+"F4.wireOp",EDGE,"E30")])]}),makeQuery(id+"F8.opExtrude","SWEPT_FACE",FACE,{"disambiguationData":[OSD([sQuery(id+"F7.wireOp",EDGE,"E67")])]})]});
            var Q3;
            {var subQ0=sQuery(id+"F4.wireOp",EDGE,"E30");Q3=makeQuery(id+"F8.boolean.opBoolean","SPLIT",EDGE,{"disambiguationData":[TD([makeQuery(id+"F5.opExtrude","SWEPT_FACE",FACE,{"disambiguationData":[OSD([sQuery(id+"F4.wireOp",EDGE,"E35.filletArc")])]})])],"derivedFrom":makeQuery(id+"F5.opExtrude","CAP_EDGE",EDGE,{"disambiguationData":[OSD([subQ0])],"isStart":false})});}
            var Q4;
            {var subQ0=sQuery(id+"F0.wireOp",EDGE,"E25.7");var subQ1=sQuery(id+"F0.wireOp",EDGE,"E25.1");var subQ2=sQuery(id+"F0.wireOp",EDGE,"E25.6");var subQ3=sQuery(id+"F0.wireOp",EDGE,"E25.5");var subQ4=sQuery(id+"F0.wireOp",EDGE,"E25.4");var subQ5=sQuery(id+"F0.wireOp",EDGE,"E25.0");var subQ6=sQuery(id+"F0.wireOp",EDGE,"E25.2");var subQ7=sQuery(id+"F0.wireOp",EDGE,"E25.3");Q4=makeQuery(id+"F8.boolean.opBoolean","INTERSECT",EDGE,{"derivedFrom":[makeQuery(id+"F5.boolean.opBoolean","SPLIT",FACE,{"disambiguationData":[TD([makeQuery(id+"F2.opExtrude","SWEPT_FACE",FACE,{"disambiguationData":[OSD([subQ5])]})])],"derivedFrom":makeQuery(id+"F3.boolean.opBoolean","COPY",FACE,{"derivedFrom":makeQuery(id+"F3.opExtrude","CAP_FACE",FACE,{"disambiguationData":[OSD([subQ5,subQ1,subQ6,subQ7,subQ4,subQ3,subQ2,subQ0])],"isStart":false})})}),makeQuery(id+"F8.opExtrude","SWEPT_FACE",FACE,{"disambiguationData":[OSD([sQuery(id+"F7.wireOp",EDGE,"E67")])]})]});}
            var Q5;
            Q5=makeQuery(id+"F8.boolean.opBoolean","INTERSECT",EDGE,{"disambiguationData":[OD(0.0)],"derivedFrom":[makeQuery(id+"F5.opExtrude","SWEPT_FACE",FACE,{"disambiguationData":[OSD([sQuery(id+"F4.wireOp",EDGE,"E30")])]}),makeQuery(id+"F8.opExtrude","SWEPT_FACE",FACE,{"disambiguationData":[OSD([sQuery(id+"F7.wireOp",EDGE,"E67")])]})]});
            fillet(context, id + "F14", {"entities" : qUnion([Q0, Q1, Q2, Q3, Q4, Q5]), "radius" : 3 * mm, "tangentPropagation" : true, "allowEdgeOverflow" : false});
        }
        {
            var Q0;
            Q0=makeQuery(id+"F1.opExtrude","CAP_EDGE",EDGE,{"disambiguationData":[OSD([sQuery(id+"F0.wireOp",EDGE,"E1.bottom")])],"isStart":false});
            fillet(context, id + "F15", {"entities" : qUnion([Q0]), "radius" : 2 * mm, "tangentPropagation" : true, "allowEdgeOverflow" : false});
        }
        {
            var Q0;
            {var subQ0=sQuery(id+"F0.wireOp",EDGE,"E22.filletArc");var subQ1=sQuery(id+"F0.wireOp",EDGE,"E7");var subQ2=sQuery(id+"F0.wireOp",EDGE,"E6");var subQ3=sQuery(id+"F0.wireOp",EDGE,"E5");var subQ4=sQuery(id+"F0.wireOp",EDGE,"E4");var subQ5=sQuery(id+"F0.wireOp",EDGE,"E1.bottom");var subQ6=sQuery(id+"F0.wireOp",EDGE,"E21.filletArc");var subQ7=sQuery(id+"F0.wireOp",EDGE,"E1.top");var subQ8=sQuery(id+"F0.wireOp",EDGE,"E1.left");var subQ9=sQuery(id+"F0.wireOp",EDGE,"E1.right");var subQ10=sQuery(id+"F0.wireOp",EDGE,"E23.filletArc");var subQ11=sQuery(id+"F0.wireOp",EDGE,"E24.filletArc");Q0=makeQuery(id+"F2.boolean.opBoolean","SPLIT",FACE,{"disambiguationData":[TD([makeQuery(id+"F1.opExtrude","SWEPT_FACE",FACE,{"disambiguationData":[OSD([subQ5])]})])],"derivedFrom":makeQuery(id+"F1.opExtrude","CAP_FACE",FACE,{"disambiguationData":[OSD([subQ5,subQ7,subQ8,subQ9,subQ4,subQ3,subQ2,subQ1,subQ6,subQ0,subQ10,subQ11])],"isStart":true})});}
            var sketch = newSketch(context, id + "F16", { "sketchPlane" : qUnion([Q0])});
            skLineSegment(sketch, "E79", {"start": v(0, 90) * mm, "end": v(0, 120) * mm, "construction": true});
            skCircle(sketch, "E80", {"center": v(0, 120) * mm, "radius": 6 * mm});
            skLineSegment(sketch, "E81", {"start": v(-33, 90) * mm, "end": v(-15, 108) * mm});
            skLineSegment(sketch, "E82", {"start": v(-15, 108) * mm, "end": v(-15, 120) * mm});
            skArc(sketch, "E83", {"start": v(15, 120) * mm, "mid": v(0, 135) * mm, "end": v(-15, 120) * mm});
            skLineSegment(sketch, "E84", {"start": v(15, 120) * mm, "end": v(15, 108) * mm});
            skLineSegment(sketch, "E85", {"start": v(15, 108) * mm, "end": v(33, 90) * mm});
            skLineSegment(sketch, "E86", {"start": v(0, -120) * mm, "end": v(0, 120) * mm, "construction": true});
            skPoint(sketch, "E86.startSnap0", {"position": v(0, 67.5) * mm});
            skLineSegment(sketch, "E87", {"start": v(-80, 0) * mm, "end": v(80, 0) * mm, "construction": true});
            skLineSegment(sketch, "E88.MirrorCS", {"start": v(-33, -90) * mm, "end": v(-15, -108) * mm});
            skLineSegment(sketch, "E89.MirrorCS", {"start": v(-15, -108) * mm, "end": v(-15, -120) * mm});
            skArc(sketch, "E90.MirrorCS", {"start": v(15, -120) * mm, "mid": v(0, -135) * mm, "end": v(-15, -120) * mm});
            skLineSegment(sketch, "E91.MirrorCS", {"start": v(15, -108) * mm, "end": v(33, -90) * mm});
            skLineSegment(sketch, "E92.MirrorCS", {"start": v(15, -120) * mm, "end": v(15, -108) * mm});
            skCircle(sketch, "E93.MirrorC", {"center": v(0, -120) * mm, "radius": 6 * mm});
            skSolve(sketch);
        }
        {
            var Q0;
            {var subQ1=sQuery(id+"F16.wireOp",EDGE,"E88.MirrorCS");Q0=makeQuery(id+"F16.imprint","IMPRINT",FACE,{"disambiguationData":[TD([[makeQuery(id+"F16.imprint","IMPRINT",EDGE,{"derivedFrom":subQ1}),1.0]])]});}
            var Q1;
            Q1=makeQuery(id+"F16.imprint","IMPRINT",FACE,{"disambiguationData":[TD([[makeQuery(id+"F16.imprint","IMPRINT",EDGE,{"derivedFrom":makeQuery(id+"F1.opExtrude","CAP_EDGE",EDGE,{"disambiguationData":[OSD([sQuery(id+"F0.wireOp",EDGE,"E1.left")])],"isStart":true})}),-1.0]])]});
            var Q2;
            Q2=makeQuery(id+"F16.imprint","IMPRINT",FACE,{"disambiguationData":[TD([[makeQuery(id+"F16.imprint","IMPRINT",EDGE,{"derivedFrom":sQuery(id+"F16.wireOp",EDGE,"E80")}),-1.0]])]});
            var Q3;
            Q3=makeQuery(id+"F2.opExtrude","CAP_FACE",FACE,{"disambiguationData":[OSD([sQuery(id+"F0.wireOp",EDGE,"E12"),sQuery(id+"F0.wireOp",EDGE,"E13"),sQuery(id+"F0.wireOp",EDGE,"E14"),sQuery(id+"F0.wireOp",EDGE,"E15"),sQuery(id+"F0.wireOp",EDGE,"E17.filletArc"),sQuery(id+"F0.wireOp",EDGE,"E18.filletArc"),sQuery(id+"F0.wireOp",EDGE,"E19.filletArc"),sQuery(id+"F0.wireOp",EDGE,"E20.filletArc"),sQuery(id+"F0.wireOp",EDGE,"E25.0"),sQuery(id+"F0.wireOp",EDGE,"E25.1"),sQuery(id+"F0.wireOp",EDGE,"E25.2"),sQuery(id+"F0.wireOp",EDGE,"E25.3"),sQuery(id+"F0.wireOp",EDGE,"E25.4"),sQuery(id+"F0.wireOp",EDGE,"E25.5"),sQuery(id+"F0.wireOp",EDGE,"E25.6"),sQuery(id+"F0.wireOp",EDGE,"E25.7")])],"isStart":false});
            extrude(context, id + "F17", {"entities" : qUnion([Q0, Q1, Q2]), "operationType" : NewBodyOperationType.ADD, "endBound" : BoundingType.UP_TO_SURFACE, "endBoundEntityFace" : qUnion([Q3]), "depth" : 25 * mm});
        }
    });
